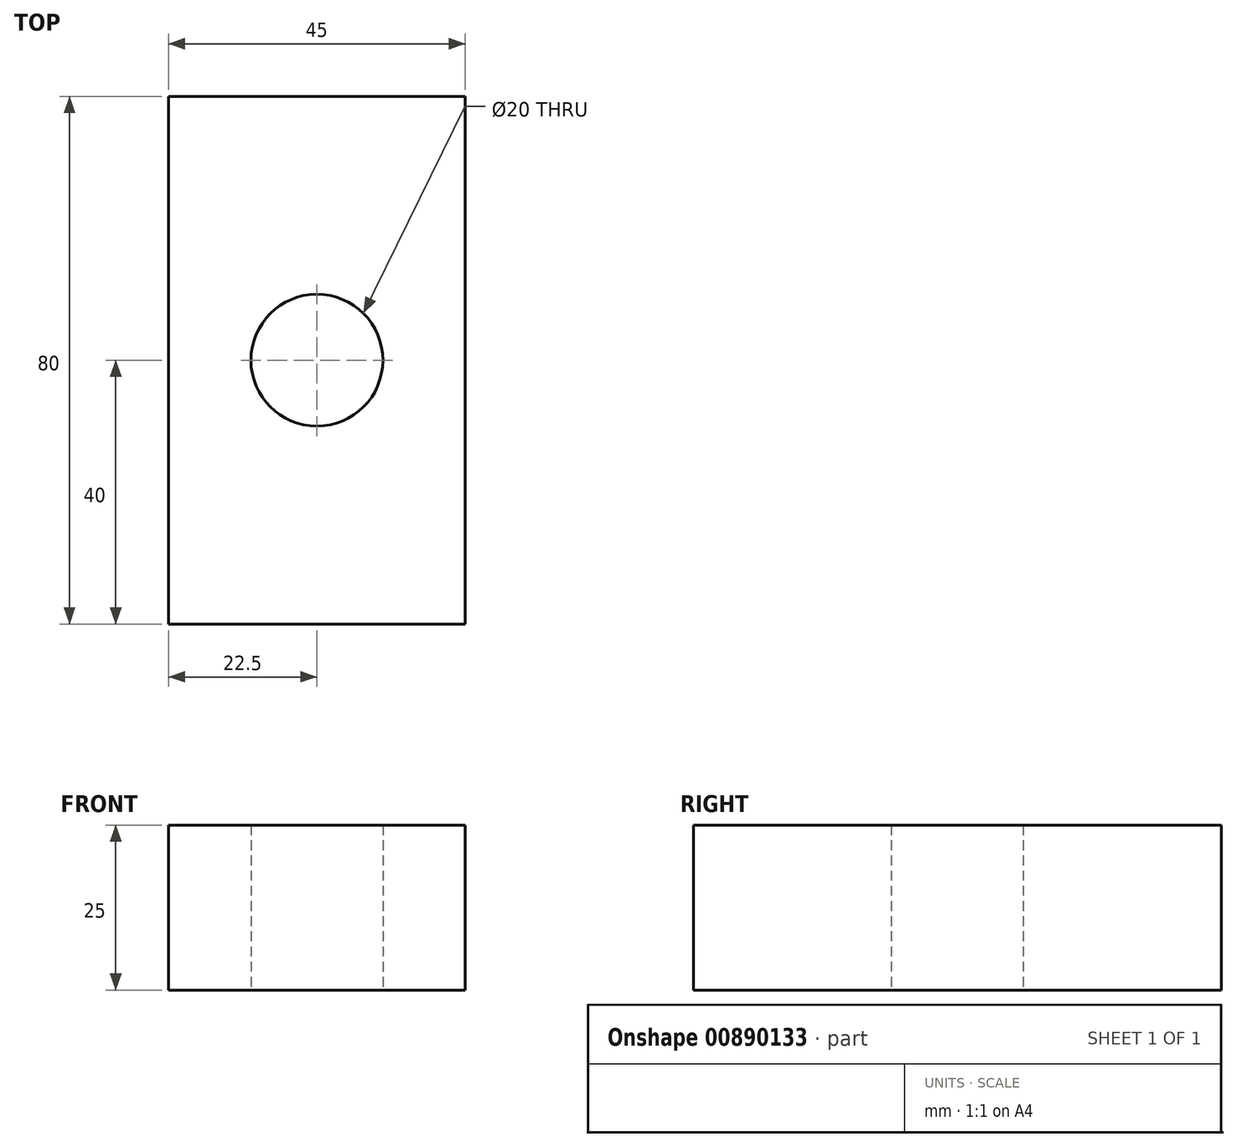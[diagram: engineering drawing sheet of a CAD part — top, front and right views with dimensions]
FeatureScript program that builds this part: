
annotation { "Feature Type Name" : "Feature", "Feature Type Description" : "" }
export const myFeature = defineFeature(function(context is Context, id is Id, definition is map)
    precondition{}
    {
        {
            var Q0;
            Q0=qCreatedBy(makeId("Top.planeOp"),FACE);
            var sketch = newSketch(context, id + "F0", { "sketchPlane" : qUnion([Q0])});
            skLineSegment(sketch, "E0.bottom", {"start": v(-22.5, 40) * mm, "end": v(22.5, 40) * mm});
            skLineSegment(sketch, "E0.top", {"start": v(-22.5, -40) * mm, "end": v(22.5, -40) * mm});
            skLineSegment(sketch, "E0.left", {"start": v(-22.5, 40) * mm, "end": v(-22.5, -40) * mm});
            skLineSegment(sketch, "E0.right", {"start": v(22.5, 40) * mm, "end": v(22.5, -40) * mm});
            skPoint(sketch, "E0.middle", {"position": v(0, 0) * mm});
            skCircle(sketch, "E1", {"center": v(0, 0) * mm, "radius": 10 * mm});
            skSolve(sketch);
        }
        {
            var Q0;
            Q0=qSketchRegion(id+"F0",true);
            extrude(context, id + "F1", {"entities" : qUnion([Q0]), "depth" : 25 * mm, "offsetDistance" : 25 * mm});
        }
    });
